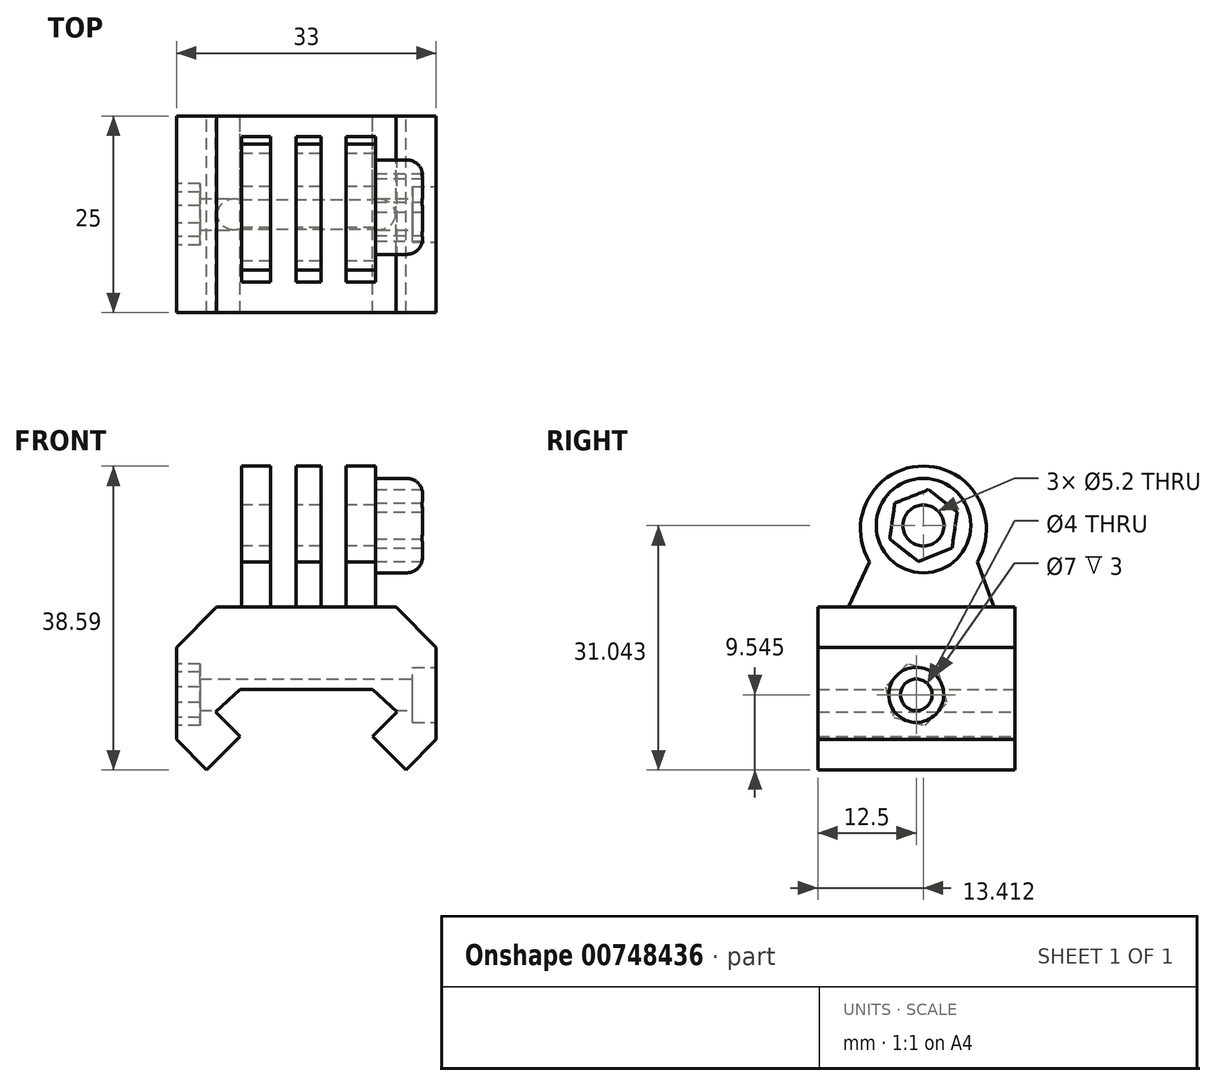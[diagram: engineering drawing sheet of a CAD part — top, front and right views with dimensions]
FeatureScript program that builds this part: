
annotation { "Feature Type Name" : "Feature", "Feature Type Description" : "" }
export const myFeature = defineFeature(function(context is Context, id is Id, definition is map)
    precondition{}
    {
        {
            var Q0;
            Q0=qCreatedBy(makeId("Front.planeOp"),FACE);
            var sketch = newSketch(context, id + "F0", { "sketchPlane" : qUnion([Q0])});
            skLineSegment(sketch, "E0", {"start": v(-8.3, 0) * mm, "end": v(8.5, 0) * mm});
            skLineSegment(sketch, "E1", {"start": v(-8.3, 0) * mm, "end": v(-11.4, -2.9) * mm});
            skLineSegment(sketch, "E2", {"start": v(-11.4, -2.9) * mm, "end": v(-8.3, -6) * mm});
            skLineSegment(sketch, "E3", {"start": v(-8.3, -6) * mm, "end": v(-12.54, -10.24) * mm});
            skLineSegment(sketch, "E4", {"start": v(-12.54, -10.24) * mm, "end": v(-22.26, -0.52) * mm});
            skLineSegment(sketch, "E5", {"start": v(-22.26, -0.52) * mm, "end": v(-11.3, 10.44) * mm});
            skLineSegment(sketch, "E6", {"start": v(-11.3, 10.44) * mm, "end": v(11.5, 10.44) * mm});
            skLineSegment(sketch, "E7", {"start": v(11.5, 10.44) * mm, "end": v(22.46, -0.52) * mm});
            skLineSegment(sketch, "E8", {"start": v(22.46, -0.52) * mm, "end": v(12.74, -10.24) * mm});
            skLineSegment(sketch, "E9", {"start": v(12.74, -10.24) * mm, "end": v(8.5, -6) * mm});
            skLineSegment(sketch, "E10", {"start": v(8.5, -6) * mm, "end": v(11.6, -2.9) * mm});
            skLineSegment(sketch, "E11", {"start": v(11.6, -2.9) * mm, "end": v(8.5, 0) * mm});
            skSolve(sketch);
        }
        {
            var Q0;
            Q0=qSketchRegion(id+"F0",true);
            extrude(context, id + "F1", {"entities" : qUnion([Q0]), "depth" : 25 * mm, "offsetDistance" : 25 * mm});
        }
        {
            var Q0;
            Q0=makeQuery(id+"F1.opExtrude","CAP_FACE",FACE,{"disambiguationData":[OSD([sQuery(id+"F0.wireOp",EDGE,"E0"),sQuery(id+"F0.wireOp",EDGE,"E1"),sQuery(id+"F0.wireOp",EDGE,"E2"),sQuery(id+"F0.wireOp",EDGE,"E3"),sQuery(id+"F0.wireOp",EDGE,"E4"),sQuery(id+"F0.wireOp",EDGE,"E5"),sQuery(id+"F0.wireOp",EDGE,"E6"),sQuery(id+"F0.wireOp",EDGE,"E7"),sQuery(id+"F0.wireOp",EDGE,"E8"),sQuery(id+"F0.wireOp",EDGE,"E9"),sQuery(id+"F0.wireOp",EDGE,"E10"),sQuery(id+"F0.wireOp",EDGE,"E11")])],"isStart":false});
            var sketch = newSketch(context, id + "F2", { "sketchPlane" : qUnion([Q0])});
            skLineSegment(sketch, "E12.bottom", {"start": v(-24, 10) * mm, "end": v(-16.4, 10) * mm});
            skLineSegment(sketch, "E12.top", {"start": v(-24, -11.1) * mm, "end": v(-16.4, -11.1) * mm});
            skLineSegment(sketch, "E12.left", {"start": v(-24, 10) * mm, "end": v(-24, -11.1) * mm});
            skLineSegment(sketch, "E12.right", {"start": v(-16.4, 10) * mm, "end": v(-16.4, -11.1) * mm});
            skLineSegment(sketch, "E13.bottom", {"start": v(26.87, 13.5) * mm, "end": v(16.6, 13.5) * mm});
            skLineSegment(sketch, "E13.top", {"start": v(26.87, -16.6) * mm, "end": v(16.6, -16.6) * mm});
            skLineSegment(sketch, "E13.left", {"start": v(26.87, 13.5) * mm, "end": v(26.87, -16.6) * mm});
            skLineSegment(sketch, "E13.right", {"start": v(16.6, 13.5) * mm, "end": v(16.6, -16.6) * mm});
            skSolve(sketch);
        }
        {
            var Q0;
            Q0=qSketchRegion(id+"F2",true);
            extrude(context, id + "F3", {"entities" : qUnion([Q0]), "operationType" : NewBodyOperationType.REMOVE, "oppositeDirection" : true, "depth" : 25 * mm, "offsetDistance" : 25 * mm});
        }
        {
            var Q0;
            Q0=makeQuery(id+"F3.boolean.opBoolean","COPY",FACE,{"derivedFrom":makeQuery(id+"F3.opExtrude","SWEPT_FACE",FACE,{"disambiguationData":[OSD([sQuery(id+"F2.wireOp",EDGE,"E13.right")])]})});
            var sketch = newSketch(context, id + "F4", { "sketchPlane" : qUnion([Q0])});
            skCircle(sketch, "E14", {"center": v(-12.5, -0.7) * mm, "radius": 2 * mm});
            skSolve(sketch);
        }
        {
            var Q0;
            Q0=qSketchRegion(id+"F4",true);
            extrude(context, id + "F5", {"entities" : qUnion([Q0]), "operationType" : NewBodyOperationType.REMOVE, "oppositeDirection" : true, "depth" : 35 * mm, "offsetDistance" : 25 * mm});
        }
        {
            var Q0;
            Q0=makeQuery(id+"F3.boolean.opBoolean","COPY",FACE,{"derivedFrom":makeQuery(id+"F3.opExtrude","SWEPT_FACE",FACE,{"disambiguationData":[OSD([sQuery(id+"F2.wireOp",EDGE,"E13.right")])]})});
            var sketch = newSketch(context, id + "F6", { "sketchPlane" : qUnion([Q0])});
            skCircle(sketch, "E15", {"center": v(-12.5, -0.7) * mm, "radius": 3.5 * mm});
            skSolve(sketch);
        }
        {
            var Q0;
            Q0=qSketchRegion(id+"F6",true);
            extrude(context, id + "F7", {"entities" : qUnion([Q0]), "operationType" : NewBodyOperationType.REMOVE, "oppositeDirection" : true, "depth" : 3 * mm, "offsetDistance" : 25 * mm});
        }
        {
            var Q0;
            Q0=makeQuery(id+"F3.boolean.opBoolean","COPY",FACE,{"derivedFrom":makeQuery(id+"F3.opExtrude","SWEPT_FACE",FACE,{"disambiguationData":[OSD([sQuery(id+"F2.wireOp",EDGE,"E12.right")])]})});
            var sketch = newSketch(context, id + "F8", { "sketchPlane" : qUnion([Q0])});
            skCircle(sketch, "E16.cCircle", {"center": v(12.5, -0.7) * mm, "radius": 3.5 * mm, "construction": true});
            skLineSegment(sketch, "E16.0", {"start": v(16.42, 0.3) * mm, "end": v(15.32, -3.59) * mm});
            skLineSegment(sketch, "E16.1", {"start": v(15.32, -3.59) * mm, "end": v(11.4, -4.59) * mm});
            skLineSegment(sketch, "E16.2", {"start": v(11.4, -4.59) * mm, "end": v(8.58, -1.7) * mm});
            skLineSegment(sketch, "E16.3", {"start": v(8.58, -1.7) * mm, "end": v(9.68, 2.2) * mm});
            skLineSegment(sketch, "E16.4", {"start": v(9.68, 2.2) * mm, "end": v(13.6, 3.2) * mm});
            skLineSegment(sketch, "E16.5", {"start": v(13.6, 3.2) * mm, "end": v(16.42, 0.3) * mm});
            skPoint(sketch, "E16.0.midPoint", {"position": v(15.87, -1.64) * mm});
            skSolve(sketch);
        }
        {
            var Q0;
            Q0=qSketchRegion(id+"F8",true);
            extrude(context, id + "F9", {"entities" : qUnion([Q0]), "operationType" : NewBodyOperationType.REMOVE, "oppositeDirection" : true, "depth" : 3 * mm, "offsetDistance" : 25 * mm});
        }
        {
            var Q0;
            Q0=makeQuery(id+"F1.opExtrude","SWEPT_FACE",FACE,{"disambiguationData":[OSD([sQuery(id+"F0.wireOp",EDGE,"E6")])]});
            var sketch = newSketch(context, id + "F10", { "sketchPlane" : qUnion([Q0])});
            skLineSegment(sketch, "E17.bottom", {"start": v(-8.13, -2.64) * mm, "end": v(8.87, -2.64) * mm});
            skLineSegment(sketch, "E17.top", {"start": v(-8.13, -21.1) * mm, "end": v(8.87, -21.1) * mm});
            skLineSegment(sketch, "E17.left", {"start": v(-8.13, -2.64) * mm, "end": v(-8.13, -21.1) * mm});
            skLineSegment(sketch, "E17.right", {"start": v(8.87, -2.64) * mm, "end": v(8.87, -21.1) * mm});
            skSolve(sketch);
        }
        {
            var Q0;
            Q0 = qSketchRegion(id + "F10", true);
            extrude(context, id + "F11", {"entities" : qUnion([Q0]), "operationType" : NewBodyOperationType.ADD, "depth" : 18 * mm, "offsetDistance" : 25 * mm});
        }
        {
            var Q0;
            Q0=makeQuery(id+"F11.opExtrude","CAP_FACE",FACE,{"disambiguationData":[OSD([sQuery(id+"F10.wireOp",EDGE,"E17.bottom"),sQuery(id+"F10.wireOp",EDGE,"E17.top"),sQuery(id+"F10.wireOp",EDGE,"E17.left"),sQuery(id+"F10.wireOp",EDGE,"E17.right")])],"isStart":false});
            var sketch = newSketch(context, id + "F12", { "sketchPlane" : qUnion([Q0])});
            skLineSegment(sketch, "E18.bottom", {"start": v(-4.43, -2.64) * mm, "end": v(-1.23, -2.64) * mm});
            skLineSegment(sketch, "E18.top", {"start": v(-4.43, -21.1) * mm, "end": v(-1.23, -21.1) * mm});
            skLineSegment(sketch, "E18.left", {"start": v(-4.43, -2.64) * mm, "end": v(-4.43, -21.1) * mm});
            skLineSegment(sketch, "E18.right", {"start": v(-1.23, -2.64) * mm, "end": v(-1.23, -21.1) * mm});
            skLineSegment(sketch, "E19.bottom", {"start": v(1.97, -2.64) * mm, "end": v(5.17, -2.64) * mm});
            skLineSegment(sketch, "E19.top", {"start": v(1.97, -21.1) * mm, "end": v(5.17, -21.1) * mm});
            skLineSegment(sketch, "E19.left", {"start": v(1.97, -2.64) * mm, "end": v(1.97, -21.1) * mm});
            skLineSegment(sketch, "E19.right", {"start": v(5.17, -2.64) * mm, "end": v(5.17, -21.1) * mm});
            skSolve(sketch);
        }
        {
            var Q0;
            Q0 = qSketchRegion(id + "F12", true);
            extrude(context, id + "F13", {"entities" : qUnion([Q0]), "operationType" : NewBodyOperationType.REMOVE, "oppositeDirection" : true, "depth" : 18 * mm, "offsetDistance" : 25 * mm});
        }
        {
            var Q0;
            Q0=makeQuery(id+"F11.opExtrude","SWEPT_FACE",FACE,{"disambiguationData":[OSD([sQuery(id+"F10.wireOp",EDGE,"E17.left")])]});
            var sketch = newSketch(context, id + "F14", { "sketchPlane" : qUnion([Q0])});
            skCircle(sketch, "E20", {"center": v(11.6, 20.35) * mm, "radius": 8 * mm});
            skLineSegment(sketch, "E21", {"start": v(4.76, 16.2) * mm, "end": v(2.64, 10.44) * mm});
            skLineSegment(sketch, "E22", {"start": v(2.64, 10.44) * mm, "end": v(21.1, 10.44) * mm});
            skLineSegment(sketch, "E23", {"start": v(21.1, 10.44) * mm, "end": v(18.43, 16.2) * mm});
            skSolve(sketch);
        }
        {
            var Q0;
            {var subQ2=sQuery(id+"F14.wireOp",EDGE,"E21");Q0=makeQuery(id+"F14.imprint","IMPRINT",FACE,{"disambiguationData":[TD([[makeQuery(id+"F14.imprint","IMPRINT",EDGE,{"derivedFrom":subQ2}),-1.0]])]});}
            extrude(context, id + "F15", {"entities" : qUnion([Q0]), "operationType" : NewBodyOperationType.REMOVE, "oppositeDirection" : true, "depth" : 25 * mm, "offsetDistance" : 25 * mm});
        }
        {
            var Q0;
            Q0=makeQuery(id+"F11.opExtrude","SWEPT_FACE",FACE,{"disambiguationData":[OSD([sQuery(id+"F10.wireOp",EDGE,"E17.left")])]});
            var sketch = newSketch(context, id + "F16", { "sketchPlane" : qUnion([Q0])});
            skCircle(sketch, "E24", {"center": v(11.59, 20.8) * mm, "radius": 2.6 * mm});
            skSolve(sketch);
        }
        {
            var Q0;
            Q0 = qSketchRegion(id + "F16", true);
            extrude(context, id + "F17", {"entities" : qUnion([Q0]), "operationType" : NewBodyOperationType.REMOVE, "oppositeDirection" : true, "depth" : 25 * mm, "offsetDistance" : 25 * mm});
        }
        {
            var Q0;
            Q0=makeQuery(id+"F11.opExtrude","SWEPT_FACE",FACE,{"disambiguationData":[OSD([sQuery(id+"F10.wireOp",EDGE,"E17.right")])]});
            var sketch = newSketch(context, id + "F18", { "sketchPlane" : qUnion([Q0])});
            skCircle(sketch, "E25", {"center": v(-11.59, 20.8) * mm, "radius": 6 * mm});
            skSolve(sketch);
        }
        {
            var Q0;
            Q0 = qSketchRegion(id + "F18", true);
            extrude(context, id + "F19", {"entities" : qUnion([Q0]), "operationType" : NewBodyOperationType.ADD, "depth" : 6 * mm, "offsetDistance" : 25 * mm});
        }
        {
            var Q0;
            Q0=makeQuery(id+"F19.opExtrude","CAP_EDGE",EDGE,{"disambiguationData":[OSD([sQuery(id+"F18.wireOp",EDGE,"E25")])],"isStart":false});
            fillet(context, id + "F20", {"entities" : qUnion([Q0]), "radius" : 2 * mm, "tangentPropagation" : true, "allowEdgeOverflow" : false});
        }
        {
            var Q0;
            Q0=makeQuery(id+"F19.opExtrude","CAP_FACE",FACE,{"disambiguationData":[OSD([sQuery(id+"F18.wireOp",EDGE,"E25")])],"isStart":false});
            var sketch = newSketch(context, id + "F21", { "sketchPlane" : qUnion([Q0])});
            skCircle(sketch, "E26.cCircle", {"center": v(-11.59, 20.8) * mm, "radius": 4 * mm, "construction": true});
            skLineSegment(sketch, "E26.0", {"start": v(-7.95, 17.95) * mm, "end": v(-12.24, 16.23) * mm});
            skLineSegment(sketch, "E26.1", {"start": v(-12.24, 16.23) * mm, "end": v(-15.87, 19.08) * mm});
            skLineSegment(sketch, "E26.2", {"start": v(-15.87, 19.08) * mm, "end": v(-15.22, 23.65) * mm});
            skLineSegment(sketch, "E26.3", {"start": v(-15.22, 23.65) * mm, "end": v(-10.94, 25.38) * mm});
            skLineSegment(sketch, "E26.4", {"start": v(-10.94, 25.38) * mm, "end": v(-7.3, 22.53) * mm});
            skLineSegment(sketch, "E26.5", {"start": v(-7.3, 22.53) * mm, "end": v(-7.95, 17.95) * mm});
            skPoint(sketch, "E26.0.midPoint", {"position": v(-10.1, 17.1) * mm});
            skSolve(sketch);
        }
        {
            var Q0;
            Q0 = qSketchRegion(id + "F21", true);
            extrude(context, id + "F22", {"entities" : qUnion([Q0]), "operationType" : NewBodyOperationType.REMOVE, "oppositeDirection" : true, "depth" : 6 * mm, "offsetDistance" : 25 * mm});
        }
    });
